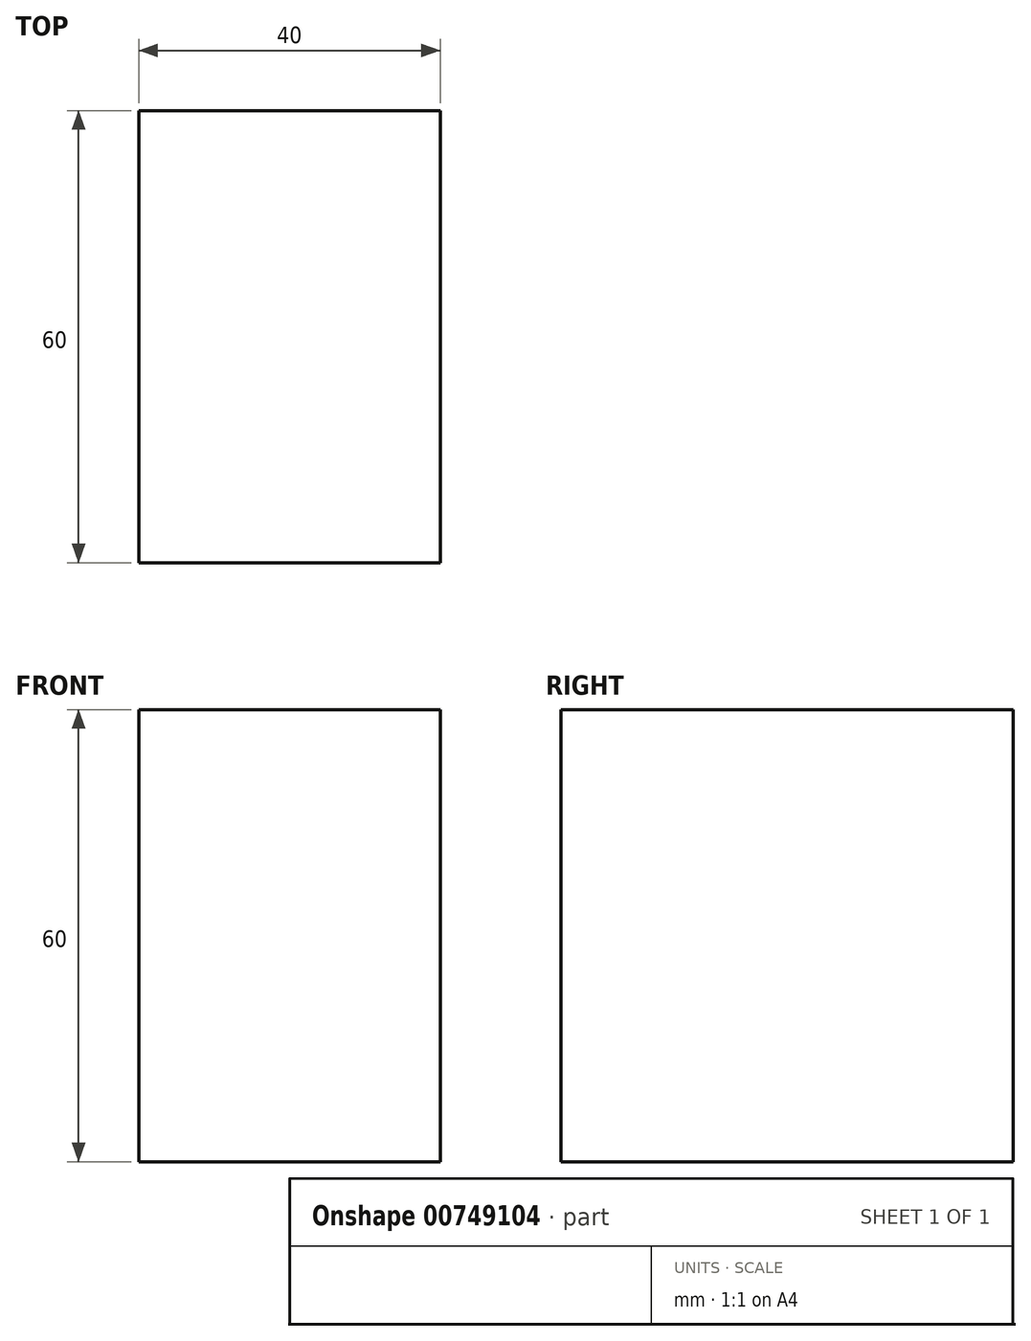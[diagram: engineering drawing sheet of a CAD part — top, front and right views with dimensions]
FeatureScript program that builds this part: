
annotation { "Feature Type Name" : "Feature", "Feature Type Description" : "" }
export const myFeature = defineFeature(function(context is Context, id is Id, definition is map)
    precondition{}
    {
        {
            var Q0;
            Q0=qCreatedBy(makeId("Top.planeOp"),FACE);
            var sketch = newSketch(context, id + "F0", { "sketchPlane" : qUnion([Q0])});
            skLineSegment(sketch, "E0", {"start": v(0, 0) * mm, "end": v(0, 60) * mm});
            skLineSegment(sketch, "E1", {"start": v(0, 60) * mm, "end": v(-40, 60) * mm});
            skLineSegment(sketch, "E2", {"start": v(-40, 60) * mm, "end": v(-40, 0) * mm});
            skLineSegment(sketch, "E3", {"start": v(-40, 0) * mm, "end": v(0, 0) * mm});
            skSolve(sketch);
        }
        {
            var Q0;
            Q0=makeQuery(id+"F0.imprint","IMPRINT",FACE,{"disambiguationData":[TD([[makeQuery(id+"F0.imprint","IMPRINT",EDGE,{"derivedFrom":sQuery(id+"F0.wireOp",EDGE,"E0")}),1.0]])]});
            extrude(context, id + "F1", {"entities" : qUnion([Q0]), "depth" : 60 * mm, "offsetDistance" : 25 * mm});
        }
    });
